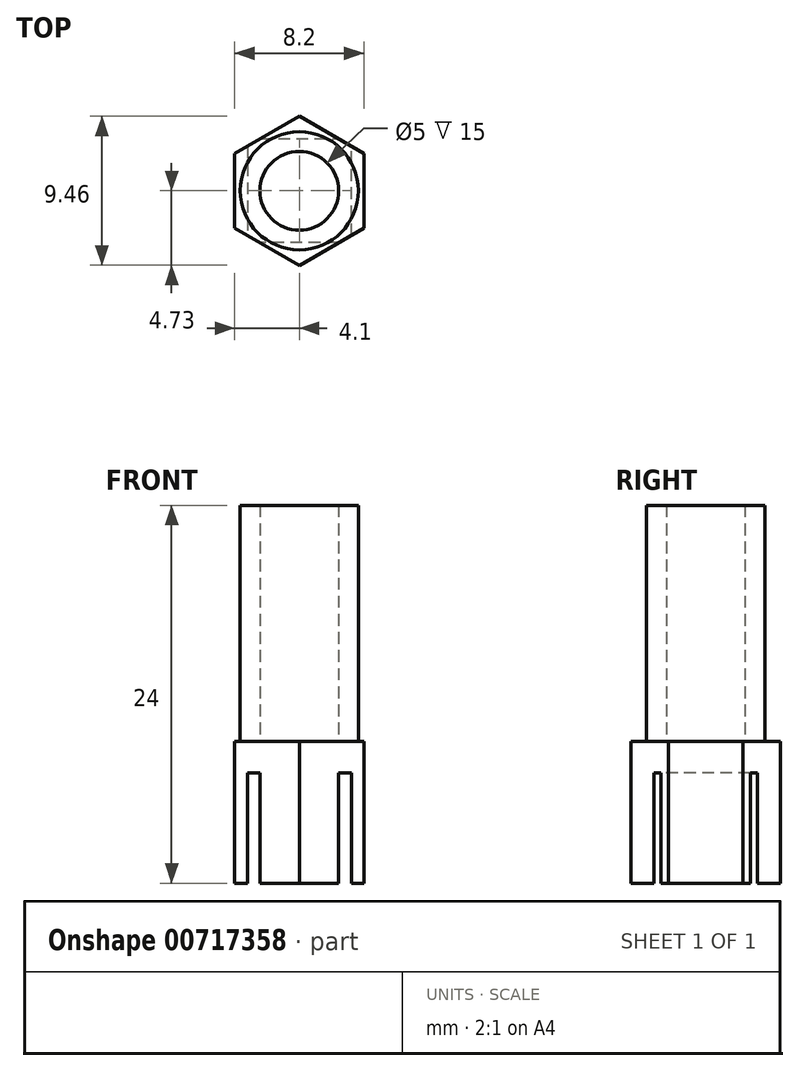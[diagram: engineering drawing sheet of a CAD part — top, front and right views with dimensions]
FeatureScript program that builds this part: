
annotation { "Feature Type Name" : "Feature", "Feature Type Description" : "" }
export const myFeature = defineFeature(function(context is Context, id is Id, definition is map)
    precondition{}
    {
        {
            var Q0;
            Q0=qCreatedBy(makeId("Top.planeOp"),FACE);
            var sketch = newSketch(context, id + "F0", { "sketchPlane" : qUnion([Q0])});
            skCircle(sketch, "E0", {"center": v(0, 0) * mm, "radius": 2.5 * mm});
            skCircle(sketch, "E1", {"center": v(0, 0) * mm, "radius": 3.75 * mm});
            skCircle(sketch, "E2.cCircle", {"center": v(0, 0) * mm, "radius": 4.1 * mm, "construction": true});
            skLineSegment(sketch, "E2.0", {"start": v(4.1, 2.37) * mm, "end": v(4.1, -2.37) * mm});
            skLineSegment(sketch, "E2.1", {"start": v(4.1, -2.37) * mm, "end": v(0, -4.73) * mm});
            skLineSegment(sketch, "E2.2", {"start": v(0, -4.73) * mm, "end": v(-4.1, -2.37) * mm});
            skLineSegment(sketch, "E2.3", {"start": v(-4.1, -2.37) * mm, "end": v(-4.1, 2.37) * mm});
            skLineSegment(sketch, "E2.4", {"start": v(-4.1, 2.37) * mm, "end": v(0, 4.73) * mm});
            skLineSegment(sketch, "E2.5", {"start": v(0, 4.73) * mm, "end": v(4.1, 2.37) * mm});
            skPoint(sketch, "E2.0.midPoint", {"position": v(4.1, 0) * mm});
            skSolve(sketch);
        }
        {
            var Q0;
            {var subQ0=sQuery(id+"F0.wireOp",EDGE,"E2.5");var subQ1=sQuery(id+"F0.wireOp",EDGE,"E1");var subQ2=makeQuery(id+"F0.imprint","INTERSECT",VERTEX,{"disambiguationData":[OD(0.0)],"derivedFrom":[subQ1,subQ0]});Q0=makeQuery(id+"F0.imprint","IMPRINT",FACE,{"disambiguationData":[TD([[makeQuery(id+"F0.imprint","IMPRINT",EDGE,{"disambiguationData":[TD([[subQ2,-1.0]])],"derivedFrom":subQ1}),1.0]])]});}
            var Q1;
            {var subQ0=sQuery(id+"F0.wireOp",EDGE,"E2.0");var subQ1=sQuery(id+"F0.wireOp",EDGE,"E1");var subQ2=makeQuery(id+"F0.imprint","INTERSECT",VERTEX,{"disambiguationData":[OD(0.0)],"derivedFrom":[subQ1,subQ0]});Q1=makeQuery(id+"F0.imprint","IMPRINT",FACE,{"disambiguationData":[TD([[makeQuery(id+"F0.imprint","IMPRINT",EDGE,{"disambiguationData":[TD([[subQ2,1.0]])],"derivedFrom":subQ1}),1.0]])]});}
            var Q2;
            Q2=makeQuery(id+"F0.imprint","IMPRINT",FACE,{"disambiguationData":[TD([[makeQuery(id+"F0.imprint","IMPRINT",EDGE,{"derivedFrom":sQuery(id+"F0.wireOp",EDGE,"E0")}),-1.0]])]});
            var Q3;
            {var subQ0=sQuery(id+"F0.wireOp",EDGE,"E2.4");var subQ1=sQuery(id+"F0.wireOp",EDGE,"E1");var subQ2=makeQuery(id+"F0.imprint","INTERSECT",VERTEX,{"disambiguationData":[OD(0.0)],"derivedFrom":[subQ1,subQ0]});Q3=makeQuery(id+"F0.imprint","IMPRINT",FACE,{"disambiguationData":[TD([[makeQuery(id+"F0.imprint","IMPRINT",EDGE,{"disambiguationData":[TD([[subQ2,-1.0]])],"derivedFrom":subQ1}),1.0]])]});}
            var Q4;
            {var subQ0=sQuery(id+"F0.wireOp",EDGE,"E2.3");var subQ1=sQuery(id+"F0.wireOp",EDGE,"E1");var subQ2=makeQuery(id+"F0.imprint","INTERSECT",VERTEX,{"disambiguationData":[OD(0.0)],"derivedFrom":[subQ1,subQ0]});Q4=makeQuery(id+"F0.imprint","IMPRINT",FACE,{"disambiguationData":[TD([[makeQuery(id+"F0.imprint","IMPRINT",EDGE,{"disambiguationData":[TD([[subQ2,-1.0]])],"derivedFrom":subQ1}),1.0]])]});}
            var Q5;
            {var subQ0=sQuery(id+"F0.wireOp",EDGE,"E2.2");var subQ1=sQuery(id+"F0.wireOp",EDGE,"E1");var subQ2=makeQuery(id+"F0.imprint","INTERSECT",VERTEX,{"disambiguationData":[OD(0.0)],"derivedFrom":[subQ1,subQ0]});Q5=makeQuery(id+"F0.imprint","IMPRINT",FACE,{"disambiguationData":[TD([[makeQuery(id+"F0.imprint","IMPRINT",EDGE,{"disambiguationData":[TD([[subQ2,-1.0]])],"derivedFrom":subQ1}),1.0]])]});}
            var Q6;
            {var subQ0=sQuery(id+"F0.wireOp",EDGE,"E2.1");var subQ1=sQuery(id+"F0.wireOp",EDGE,"E1");var subQ2=makeQuery(id+"F0.imprint","INTERSECT",VERTEX,{"disambiguationData":[OD(0.0)],"derivedFrom":[subQ1,subQ0]});Q6=makeQuery(id+"F0.imprint","IMPRINT",FACE,{"disambiguationData":[TD([[makeQuery(id+"F0.imprint","IMPRINT",EDGE,{"disambiguationData":[TD([[subQ2,-1.0]])],"derivedFrom":subQ1}),1.0]])]});}
            extrude(context, id + "F1", {"entities" : qUnion([Q0, Q1, Q2, Q3, Q4, Q5, Q6]), "depth" : 15 * mm, "offsetDistance" : 25 * mm});
        }
        {
            var Q0;
            {var subQ0=sQuery(id+"F0.wireOp",EDGE,"E2.4");var subQ1=sQuery(id+"F0.wireOp",EDGE,"E1");var subQ2=makeQuery(id+"F0.imprint","INTERSECT",VERTEX,{"disambiguationData":[OD(1.0)],"derivedFrom":[subQ1,subQ0]});Q0=makeQuery(id+"F0.imprint","IMPRINT",FACE,{"disambiguationData":[TD([[makeQuery(id+"F0.imprint","IMPRINT",EDGE,{"disambiguationData":[TD([[subQ2,-1.0]])],"derivedFrom":subQ1}),-1.0]])]});}
            var Q1;
            Q1=makeQuery(id+"F0.imprint","IMPRINT",FACE,{"disambiguationData":[TD([[makeQuery(id+"F0.imprint","IMPRINT",EDGE,{"derivedFrom":sQuery(id+"F0.wireOp",EDGE,"E0")}),-1.0]])]});
            var Q2;
            {var subQ0=sQuery(id+"F0.wireOp",EDGE,"E2.5");var subQ1=sQuery(id+"F0.wireOp",EDGE,"E1");var subQ2=makeQuery(id+"F0.imprint","INTERSECT",VERTEX,{"disambiguationData":[OD(1.0)],"derivedFrom":[subQ1,subQ0]});Q2=makeQuery(id+"F0.imprint","IMPRINT",FACE,{"disambiguationData":[TD([[makeQuery(id+"F0.imprint","IMPRINT",EDGE,{"disambiguationData":[TD([[subQ2,-1.0]])],"derivedFrom":subQ1}),-1.0]])]});}
            var Q3;
            {var subQ0=sQuery(id+"F0.wireOp",EDGE,"E2.5");var subQ1=sQuery(id+"F0.wireOp",EDGE,"E1");var subQ2=makeQuery(id+"F0.imprint","INTERSECT",VERTEX,{"disambiguationData":[OD(0.0)],"derivedFrom":[subQ1,subQ0]});Q3=makeQuery(id+"F0.imprint","IMPRINT",FACE,{"disambiguationData":[TD([[makeQuery(id+"F0.imprint","IMPRINT",EDGE,{"disambiguationData":[TD([[subQ2,1.0]])],"derivedFrom":subQ1}),-1.0]])]});}
            var Q4;
            {var subQ0=sQuery(id+"F0.wireOp",EDGE,"E2.1");var subQ1=sQuery(id+"F0.wireOp",EDGE,"E1");var subQ2=makeQuery(id+"F0.imprint","INTERSECT",VERTEX,{"disambiguationData":[OD(1.0)],"derivedFrom":[subQ1,subQ0]});Q4=makeQuery(id+"F0.imprint","IMPRINT",FACE,{"disambiguationData":[TD([[makeQuery(id+"F0.imprint","IMPRINT",EDGE,{"disambiguationData":[TD([[subQ2,-1.0]])],"derivedFrom":subQ1}),-1.0]])]});}
            var Q5;
            {var subQ0=sQuery(id+"F0.wireOp",EDGE,"E2.2");var subQ1=sQuery(id+"F0.wireOp",EDGE,"E1");var subQ2=makeQuery(id+"F0.imprint","INTERSECT",VERTEX,{"disambiguationData":[OD(1.0)],"derivedFrom":[subQ1,subQ0]});Q5=makeQuery(id+"F0.imprint","IMPRINT",FACE,{"disambiguationData":[TD([[makeQuery(id+"F0.imprint","IMPRINT",EDGE,{"disambiguationData":[TD([[subQ2,-1.0]])],"derivedFrom":subQ1}),-1.0]])]});}
            var Q6;
            {var subQ0=sQuery(id+"F0.wireOp",EDGE,"E2.3");var subQ1=sQuery(id+"F0.wireOp",EDGE,"E1");var subQ2=makeQuery(id+"F0.imprint","INTERSECT",VERTEX,{"disambiguationData":[OD(1.0)],"derivedFrom":[subQ1,subQ0]});Q6=makeQuery(id+"F0.imprint","IMPRINT",FACE,{"disambiguationData":[TD([[makeQuery(id+"F0.imprint","IMPRINT",EDGE,{"disambiguationData":[TD([[subQ2,-1.0]])],"derivedFrom":subQ1}),-1.0]])]});}
            var Q7;
            Q7=makeQuery(id+"F0.imprint","IMPRINT",FACE,{"disambiguationData":[TD([[makeQuery(id+"F0.imprint","IMPRINT",EDGE,{"derivedFrom":sQuery(id+"F0.wireOp",EDGE,"E0")}),1.0]])]});
            extrude(context, id + "F2", {"entities" : qUnion([Q0, Q1, Q2, Q3, Q4, Q5, Q6, Q7]), "operationType" : NewBodyOperationType.ADD, "oppositeDirection" : true, "depth" : 9 * mm, "offsetDistance" : 25 * mm});
        }
        {
            var Q0;
            Q0=makeQuery(id+"F2.opExtrude","CAP_FACE",FACE,{"disambiguationData":[OSD([sQuery(id+"F0.wireOp",EDGE,"E2.0"),sQuery(id+"F0.wireOp",EDGE,"E2.1"),sQuery(id+"F0.wireOp",EDGE,"E2.2"),sQuery(id+"F0.wireOp",EDGE,"E2.3"),sQuery(id+"F0.wireOp",EDGE,"E2.4"),sQuery(id+"F0.wireOp",EDGE,"E2.5")])],"isStart":false});
            var sketch = newSketch(context, id + "F3", { "sketchPlane" : qUnion([Q0])});
            skLineSegment(sketch, "E3", {"start": v(0, 0) * mm, "end": v(-3.3, 0) * mm});
            skLineSegment(sketch, "E4", {"start": v(-3.3, 0) * mm, "end": v(-3.3, 3.3) * mm});
            skLineSegment(sketch, "E5", {"start": v(-3.3, 3.3) * mm, "end": v(0, 3.3) * mm});
            skLineSegment(sketch, "E6", {"start": v(0, 3.3) * mm, "end": v(0, 2.63) * mm});
            skLineSegment(sketch, "E7.MirrorCS", {"start": v(3.3, 3.3) * mm, "end": v(0, 3.3) * mm});
            skLineSegment(sketch, "E8.MirrorCS", {"start": v(3.3, 0) * mm, "end": v(3.3, 3.3) * mm});
            skLineSegment(sketch, "E9.MirrorCS", {"start": v(-3.3, 0) * mm, "end": v(-3.3, -3.3) * mm});
            skLineSegment(sketch, "E10.MirrorCS", {"start": v(-3.3, -3.3) * mm, "end": v(0, -3.3) * mm});
            skLineSegment(sketch, "E11.MirrorCS", {"start": v(3.3, -3.3) * mm, "end": v(0, -3.3) * mm});
            skLineSegment(sketch, "E12.MirrorCS", {"start": v(3.3, 0) * mm, "end": v(3.3, -3.3) * mm});
            skSolve(sketch);
        }
        {
            var Q0;
            {var subQ0=sQuery(id+"F3.wireOp",EDGE,"E4");var subQ5=sQuery(id+"F3.wireOp",EDGE,"E9.MirrorCS");var subQ6=makeQuery(id+"F3.imprint","INTERSECT",VERTEX,{"derivedFrom":[subQ0,subQ5]});Q0=makeQuery(id+"F3.imprint","IMPRINT",FACE,{"disambiguationData":[TD([[makeQuery(id+"F3.imprint","IMPRINT",EDGE,{"disambiguationData":[TD([[subQ6,-1.0]])],"derivedFrom":subQ0}),-1.0]])]});}
            extrude(context, id + "F4", {"entities" : qUnion([Q0]), "operationType" : NewBodyOperationType.REMOVE, "oppositeDirection" : true, "depth" : 7 * mm, "offsetDistance" : 25 * mm});
        }
    });
